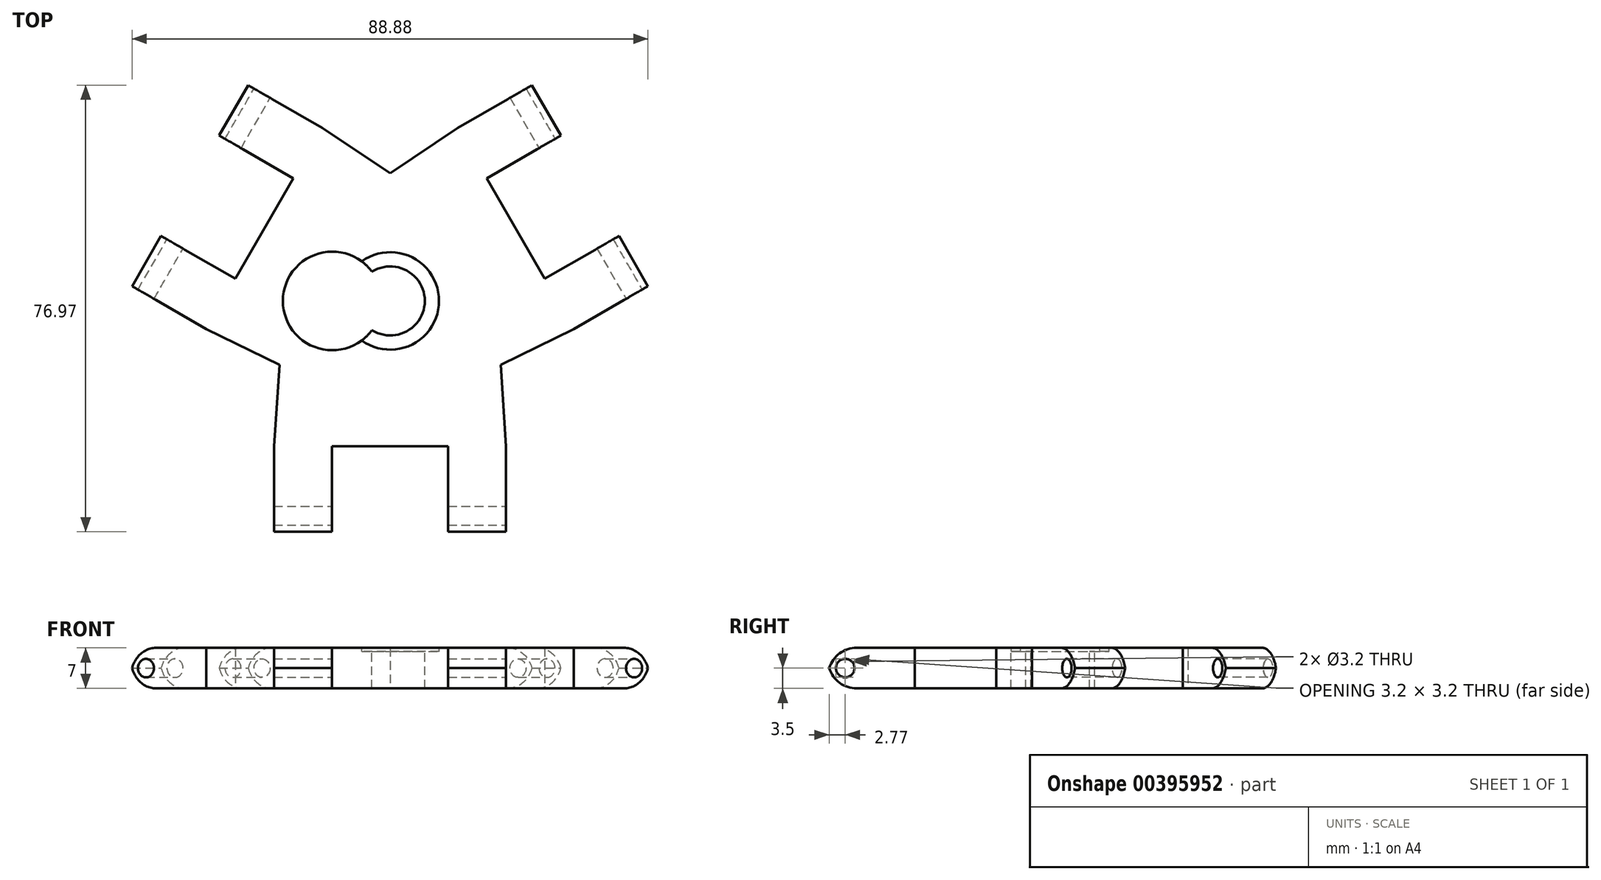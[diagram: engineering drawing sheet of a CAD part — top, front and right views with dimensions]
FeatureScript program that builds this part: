
annotation { "Feature Type Name" : "Feature", "Feature Type Description" : "" }
export const myFeature = defineFeature(function(context is Context, id is Id, definition is map)
    precondition{}
    {
        {
            var Q0;
            Q0=qCreatedBy(makeId("Top.planeOp"),FACE);
            var sketch = newSketch(context, id + "F0", { "sketchPlane" : qUnion([Q0])});
            skLineSegment(sketch, "E0", {"start": v(-0.04, -0.02) * mm, "end": v(-21.7, 12.48) * mm});
            skLineSegment(sketch, "E1", {"start": v(-21.7, 12.48) * mm, "end": v(-11.7, 29.8) * mm});
            skLineSegment(sketch, "E2", {"start": v(-21.7, 12.48) * mm, "end": v(-31.7, -4.84) * mm});
            skLineSegment(sketch, "E3", {"start": v(-0.04, -0.02) * mm, "end": v(21.6, 12.48) * mm});
            skLineSegment(sketch, "E4", {"start": v(-0.04, -0.02) * mm, "end": v(-0.04, -25.02) * mm});
            skLineSegment(sketch, "E5", {"start": v(-0.04, -25.02) * mm, "end": v(-20.04, -25.02) * mm});
            skLineSegment(sketch, "E6", {"start": v(-0.04, -25.02) * mm, "end": v(19.96, -25.02) * mm});
            skLineSegment(sketch, "E7", {"start": v(21.6, 12.48) * mm, "end": v(31.6, -4.84) * mm});
            skLineSegment(sketch, "E8", {"start": v(21.6, 12.48) * mm, "end": v(11.6, 29.8) * mm});
            skLineSegment(sketch, "E9.bottom", {"start": v(-31.7, -4.84) * mm, "end": v(-26.7, 3.82) * mm});
            skLineSegment(sketch, "E9.top", {"start": v(-44.68, 2.66) * mm, "end": v(-39.68, 11.32) * mm});
            skLineSegment(sketch, "E9.left", {"start": v(-31.7, -4.84) * mm, "end": v(-44.68, 2.66) * mm});
            skLineSegment(sketch, "E9.right", {"start": v(-26.7, 3.82) * mm, "end": v(-39.68, 11.32) * mm});
            skLineSegment(sketch, "E10.bottom", {"start": v(-11.7, 29.8) * mm, "end": v(-16.7, 21.14) * mm});
            skLineSegment(sketch, "E10.top", {"start": v(-24.68, 37.3) * mm, "end": v(-29.68, 28.64) * mm});
            skLineSegment(sketch, "E10.left", {"start": v(-11.7, 29.8) * mm, "end": v(-24.68, 37.3) * mm});
            skLineSegment(sketch, "E10.right", {"start": v(-16.7, 21.14) * mm, "end": v(-29.68, 28.64) * mm});
            skLineSegment(sketch, "E11", {"start": v(-20.04, -25.02) * mm, "end": v(-20.04, -40.02) * mm});
            skLineSegment(sketch, "E12", {"start": v(-20.04, -40.02) * mm, "end": v(-10.04, -40.02) * mm});
            skLineSegment(sketch, "E13", {"start": v(-10.04, -40.02) * mm, "end": v(-10.04, -25.02) * mm});
            skLineSegment(sketch, "E14", {"start": v(19.96, -25.02) * mm, "end": v(19.96, -40.02) * mm});
            skLineSegment(sketch, "E15", {"start": v(19.96, -40.02) * mm, "end": v(9.96, -40.02) * mm});
            skLineSegment(sketch, "E16", {"start": v(9.96, -40.02) * mm, "end": v(9.96, -25.02) * mm});
            skLineSegment(sketch, "E17", {"start": v(31.6, -4.84) * mm, "end": v(44.6, 2.66) * mm});
            skLineSegment(sketch, "E18", {"start": v(44.6, 2.66) * mm, "end": v(39.6, 11.32) * mm});
            skLineSegment(sketch, "E19", {"start": v(39.6, 11.32) * mm, "end": v(26.6, 3.82) * mm});
            skLineSegment(sketch, "E20", {"start": v(11.6, 29.8) * mm, "end": v(24.6, 37.3) * mm});
            skLineSegment(sketch, "E21", {"start": v(24.6, 37.3) * mm, "end": v(29.6, 28.64) * mm});
            skLineSegment(sketch, "E22", {"start": v(29.6, 28.64) * mm, "end": v(16.6, 21.14) * mm});
            skLineSegment(sketch, "E23", {"start": v(-0.04, -0.02) * mm, "end": v(-19.1, -11.02) * mm});
            skLineSegment(sketch, "E24", {"start": v(-0.04, -0.02) * mm, "end": v(-0.04, 21.98) * mm});
            skLineSegment(sketch, "E25", {"start": v(-0.04, -0.02) * mm, "end": v(19.01, -11.02) * mm});
            skLineSegment(sketch, "E26", {"start": v(19.01, -11.02) * mm, "end": v(31.6, -4.84) * mm});
            skLineSegment(sketch, "E27", {"start": v(19.96, -25.02) * mm, "end": v(19.01, -11.02) * mm});
            skLineSegment(sketch, "E28", {"start": v(-20.04, -25.02) * mm, "end": v(-19.1, -11.02) * mm});
            skLineSegment(sketch, "E29", {"start": v(-31.7, -4.84) * mm, "end": v(-19.1, -11.02) * mm});
            skLineSegment(sketch, "E30", {"start": v(-11.7, 29.8) * mm, "end": v(-0.04, 21.98) * mm});
            skLineSegment(sketch, "E31", {"start": v(11.6, 29.8) * mm, "end": v(-0.04, 21.98) * mm});
            skSolve(sketch);
        }
        {
            var Q0;
            Q0=qSketchRegion(id+"F0",true);
            extrude(context, id + "F1", {"entities" : qUnion([Q0]), "depth" : 7 * mm});
        }
        {
            var Q0;
            Q0=makeQuery(id+"F1.opExtrude","SWEPT_FACE",FACE,{"disambiguationData":[OSD([sQuery(id+"F0.wireOp",EDGE,"E14")])]});
            var sketch = newSketch(context, id + "F2", { "sketchPlane" : qUnion([Q0])});
            skLineSegment(sketch, "E32", {"start": v(-40.02, 3.5) * mm, "end": v(-37.02, 3.5) * mm});
            skCircle(sketch, "E33", {"center": v(-37.02, 3.5) * mm, "radius": 1.6 * mm});
            skSolve(sketch);
        }
        {
            var Q0;
            {var subQ0=sQuery(id+"F2.wireOp",EDGE,"hwxsNGN8-YZ7C-MMK4-pKxF-B9U5Xw8N2g3O");var subQ1=sQuery(id+"F2.wireOp",EDGE,"aEPsG9ev-R9g6-eiI9-y869-0mmje5FJimsM");var subQ2=makeQuery(id+"F2.imprint","INTERSECT",VERTEX,{"disambiguationData":[OD(0.0)],"derivedFrom":[subQ1,subQ0]});Q0=makeQuery(id+"F2.imprint","IMPRINT",FACE,{"disambiguationData":[TD([[makeQuery(id+"F2.imprint","IMPRINT",EDGE,{"disambiguationData":[TD([[subQ2,-1.0]])],"derivedFrom":subQ1}),1.0]])]});}
            var Q1;
            Q1=makeQuery(id+"F2.imprint","IMPRINT",FACE,{"disambiguationData":[TD([[makeQuery(id+"F2.imprint","IMPRINT",EDGE,{"derivedFrom":sQuery(id+"F2.wireOp",EDGE,"E33")}),1.0]])]});
            extrude(context, id + "F3", {"entities" : qUnion([Q0, Q1]), "operationType" : NewBodyOperationType.REMOVE, "oppositeDirection" : true, "depth" : 60 * mm});
        }
        {
            var Q0;
            Q0=makeQuery(id+"F1.opExtrude","SWEPT_FACE",FACE,{"disambiguationData":[OSD([sQuery(id+"F0.wireOp",EDGE,"E17")])]});
            var sketch = newSketch(context, id + "F4", { "sketchPlane" : qUnion([Q0])});
            skLineSegment(sketch, "E34", {"start": v(39.95, 3.5) * mm, "end": v(36.95, 3.5) * mm});
            skCircle(sketch, "E35", {"center": v(36.95, 3.5) * mm, "radius": 1.6 * mm});
            skSolve(sketch);
        }
        {
            var Q0;
            Q0=qSketchRegion(id+"F4",true);
            extrude(context, id + "F5", {"entities" : qUnion([Q0]), "operationType" : NewBodyOperationType.REMOVE, "oppositeDirection" : true, "depth" : 60 * mm});
        }
        {
            var Q0;
            Q0=makeQuery(id+"F1.opExtrude","SWEPT_FACE",FACE,{"disambiguationData":[OSD([sQuery(id+"F0.wireOp",EDGE,"E10.left")])]});
            var sketch = newSketch(context, id + "F6", { "sketchPlane" : qUnion([Q0])});
            skLineSegment(sketch, "E36", {"start": v(40.03, 3.5) * mm, "end": v(37.03, 3.5) * mm});
            skCircle(sketch, "E37", {"center": v(37.03, 3.5) * mm, "radius": 1.6 * mm});
            skSolve(sketch);
        }
        {
            var Q0;
            Q0=makeQuery(id+"F6.imprint","IMPRINT",FACE,{"disambiguationData":[TD([[makeQuery(id+"F6.imprint","IMPRINT",EDGE,{"derivedFrom":sQuery(id+"F6.wireOp",EDGE,"E37")}),1.0]])]});
            extrude(context, id + "F7", {"entities" : qUnion([Q0]), "operationType" : NewBodyOperationType.REMOVE, "oppositeDirection" : true, "depth" : 60 * mm});
        }
        {
            var Q0;
            Q0=makeQuery(id+"F1.opExtrude","CAP_EDGE",EDGE,{"disambiguationData":[OSD([sQuery(id+"F0.wireOp",EDGE,"E12")])],"isStart":false});
            var Q1;
            Q1=makeQuery(id+"F1.opExtrude","CAP_EDGE",EDGE,{"disambiguationData":[OSD([sQuery(id+"F0.wireOp",EDGE,"E12")])],"isStart":true});
            var Q2;
            Q2=makeQuery(id+"F1.opExtrude","CAP_EDGE",EDGE,{"disambiguationData":[OSD([sQuery(id+"F0.wireOp",EDGE,"E15")])],"isStart":true});
            var Q3;
            Q3=makeQuery(id+"F1.opExtrude","CAP_EDGE",EDGE,{"disambiguationData":[OSD([sQuery(id+"F0.wireOp",EDGE,"E15")])],"isStart":false});
            var Q4;
            Q4=makeQuery(id+"F1.opExtrude","CAP_EDGE",EDGE,{"disambiguationData":[OSD([sQuery(id+"F0.wireOp",EDGE,"E18")])],"isStart":false});
            var Q5;
            Q5=makeQuery(id+"F1.opExtrude","CAP_EDGE",EDGE,{"disambiguationData":[OSD([sQuery(id+"F0.wireOp",EDGE,"E18")])],"isStart":true});
            var Q6;
            Q6=makeQuery(id+"F1.opExtrude","CAP_EDGE",EDGE,{"disambiguationData":[OSD([sQuery(id+"F0.wireOp",EDGE,"E21")])],"isStart":false});
            var Q7;
            Q7=makeQuery(id+"F1.opExtrude","CAP_EDGE",EDGE,{"disambiguationData":[OSD([sQuery(id+"F0.wireOp",EDGE,"E21")])],"isStart":true});
            var Q8;
            Q8=makeQuery(id+"F1.opExtrude","CAP_EDGE",EDGE,{"disambiguationData":[OSD([sQuery(id+"F0.wireOp",EDGE,"E10.top")])],"isStart":false});
            var Q9;
            Q9=makeQuery(id+"F1.opExtrude","CAP_EDGE",EDGE,{"disambiguationData":[OSD([sQuery(id+"F0.wireOp",EDGE,"E10.top")])],"isStart":true});
            var Q10;
            Q10=makeQuery(id+"F1.opExtrude","CAP_EDGE",EDGE,{"disambiguationData":[OSD([sQuery(id+"F0.wireOp",EDGE,"E9.top")])],"isStart":false});
            var Q11;
            Q11=makeQuery(id+"F1.opExtrude","CAP_EDGE",EDGE,{"disambiguationData":[OSD([sQuery(id+"F0.wireOp",EDGE,"E9.top")])],"isStart":true});
            fillet(context, id + "F8", {"entities" : qUnion([Q0, Q1, Q2, Q3, Q4, Q5, Q6, Q7, Q8, Q9, Q10, Q11]), "radius" : 5 * mm, "tangentPropagation" : true, "allowEdgeOverflow" : false});
        }
        {
            var Q0;
            Q0=makeQuery(id+"F1.opExtrude","CAP_FACE",FACE,{"disambiguationData":[OSD([sQuery(id+"F0.wireOp",EDGE,"E1"),sQuery(id+"F0.wireOp",EDGE,"E2"),sQuery(id+"F0.wireOp",EDGE,"E5"),sQuery(id+"F0.wireOp",EDGE,"E6"),sQuery(id+"F0.wireOp",EDGE,"E7"),sQuery(id+"F0.wireOp",EDGE,"E8"),sQuery(id+"F0.wireOp",EDGE,"E9.top"),sQuery(id+"F0.wireOp",EDGE,"E9.left"),sQuery(id+"F0.wireOp",EDGE,"E9.right"),sQuery(id+"F0.wireOp",EDGE,"E10.top"),sQuery(id+"F0.wireOp",EDGE,"E10.left"),sQuery(id+"F0.wireOp",EDGE,"E10.right"),sQuery(id+"F0.wireOp",EDGE,"E11"),sQuery(id+"F0.wireOp",EDGE,"E12"),sQuery(id+"F0.wireOp",EDGE,"E13"),sQuery(id+"F0.wireOp",EDGE,"E14"),sQuery(id+"F0.wireOp",EDGE,"E15"),sQuery(id+"F0.wireOp",EDGE,"E16"),sQuery(id+"F0.wireOp",EDGE,"E17"),sQuery(id+"F0.wireOp",EDGE,"E18"),sQuery(id+"F0.wireOp",EDGE,"E19"),sQuery(id+"F0.wireOp",EDGE,"E20"),sQuery(id+"F0.wireOp",EDGE,"E21"),sQuery(id+"F0.wireOp",EDGE,"E22"),sQuery(id+"F0.wireOp",EDGE,"E26"),sQuery(id+"F0.wireOp",EDGE,"E27"),sQuery(id+"F0.wireOp",EDGE,"E28"),sQuery(id+"F0.wireOp",EDGE,"E29"),sQuery(id+"F0.wireOp",EDGE,"E30"),sQuery(id+"F0.wireOp",EDGE,"E31")])],"isStart":false});
            var sketch = newSketch(context, id + "F9", { "sketchPlane" : qUnion([Q0])});
            skSolve(sketch);
        }
        {
            var Q0;
            {var subQ9=sQuery(id+"F0.wireOp",EDGE,"E26");Q0=makeQuery(id+"F9.imprint","IMPRINT",FACE,{"disambiguationData":[TD([[makeQuery(id+"F9.imprint","IMPRINT",EDGE,{"derivedFrom":makeQuery(id+"F1.opExtrude","CAP_EDGE",EDGE,{"disambiguationData":[OSD([subQ9])],"isStart":false})}),1.0]])]});}
            var sketch = newSketch(context, id + "F10", { "sketchPlane" : qUnion([Q0])});
            skLineSegment(sketch, "E38", {"start": v(0, 0) * mm, "end": v(-10, 0) * mm});
            skCircle(sketch, "E39", {"center": v(0, 0) * mm, "radius": 5.95 * mm});
            skCircle(sketch, "E40", {"center": v(-10, 0) * mm, "radius": 8.5 * mm});
            skSolve(sketch);
        }
        {
            var Q0;
            Q0=qSketchRegion(id+"F10",true);
            extrude(context, id + "F11", {"entities" : qUnion([Q0]), "operationType" : NewBodyOperationType.REMOVE, "oppositeDirection" : true, "depth" : 25 * mm});
        }
        {
            var Q0;
            {var subQ9=sQuery(id+"F0.wireOp",EDGE,"E26");Q0=makeQuery(id+"F9.imprint","IMPRINT",FACE,{"disambiguationData":[TD([[makeQuery(id+"F9.imprint","IMPRINT",EDGE,{"derivedFrom":makeQuery(id+"F1.opExtrude","CAP_EDGE",EDGE,{"disambiguationData":[OSD([subQ9])],"isStart":false})}),1.0]])]});}
            var sketch = newSketch(context, id + "F12", { "sketchPlane" : qUnion([Q0])});
            skCircle(sketch, "E41", {"center": v(0, 0) * mm, "radius": 8.4 * mm});
            skSolve(sketch);
        }
        {
            var Q0;
            Q0=qSketchRegion(id+"F12",true);
            extrude(context, id + "F13", {"entities" : qUnion([Q0]), "operationType" : NewBodyOperationType.REMOVE, "oppositeDirection" : true, "depth" : .6 * mm});
        }
    });
